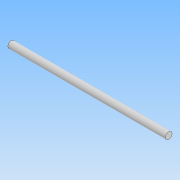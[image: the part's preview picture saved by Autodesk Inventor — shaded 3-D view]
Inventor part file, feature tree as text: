
AUTODESK INVENTOR PART (.ipt)
format: ipt  version: 2021 (Build 250183000, 183)  size: 72,192 bytes
history: native  units: mm
features: other x1, extrude x1, sketch x1
ambient origin geometry x8: Origin, YZ Plane, XZ Plane, XY Plane, X Axis, Y Axis, Z Axis, Center Point
bodies: Body1 (feature_tree)
feature tree (3):
  other  "實體1"
  extrude  "擠出1"  Depth=30.0mm
  sketch  "草圖1"
